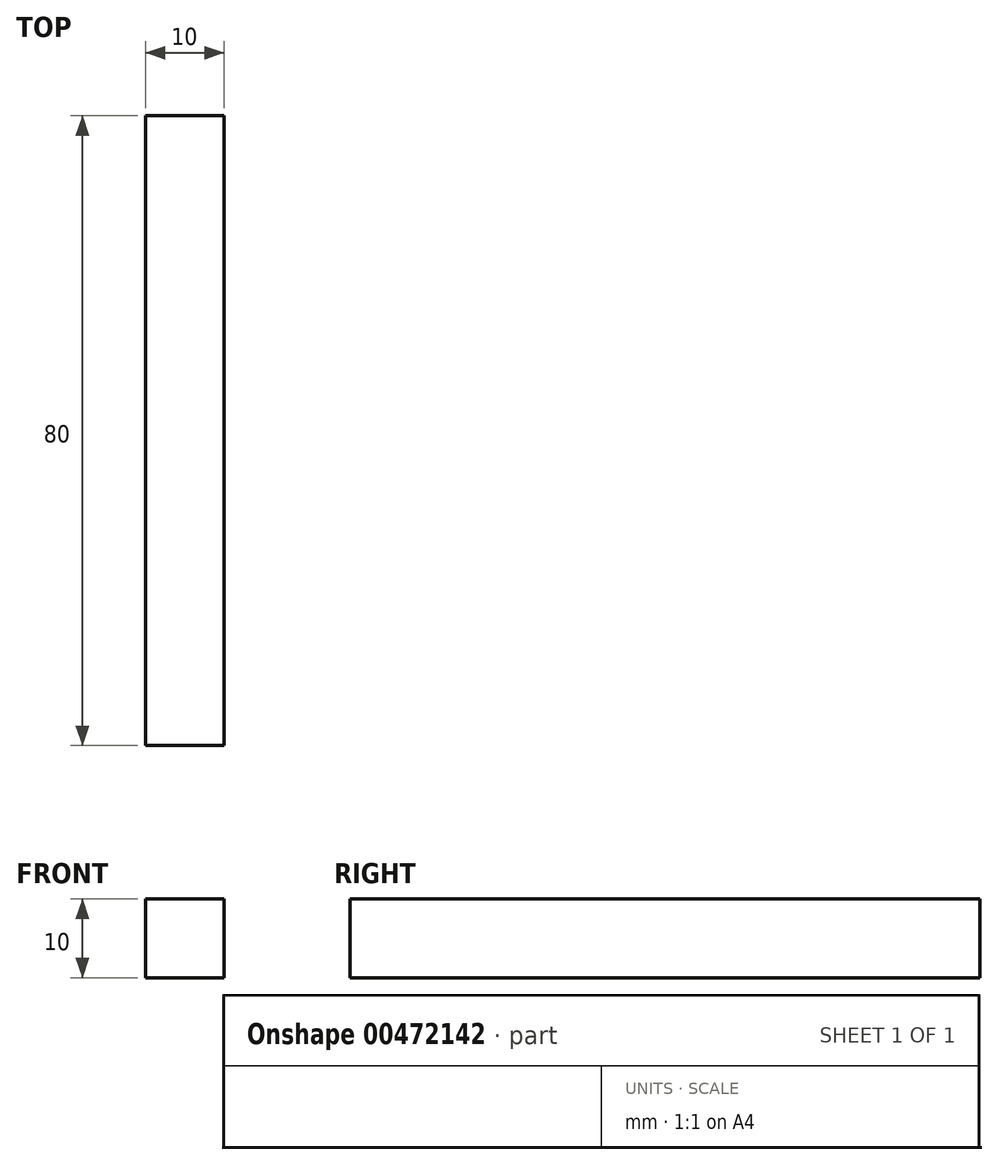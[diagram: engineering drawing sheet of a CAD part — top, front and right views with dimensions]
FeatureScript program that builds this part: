
annotation { "Feature Type Name" : "Feature", "Feature Type Description" : "" }
export const myFeature = defineFeature(function(context is Context, id is Id, definition is map)
    precondition{}
    {
        {
            var Q0;
            Q0=qCreatedBy(makeId("Front.planeOp"),FACE);
            var sketch = newSketch(context, id + "F0", { "sketchPlane" : qUnion([Q0])});
            skLineSegment(sketch, "E0.bottom", {"start": v(5, -5) * mm, "end": v(-5, -5) * mm});
            skLineSegment(sketch, "E0.top", {"start": v(5, 5) * mm, "end": v(-5, 5) * mm});
            skLineSegment(sketch, "E0.left", {"start": v(5, -5) * mm, "end": v(5, 5) * mm});
            skLineSegment(sketch, "E0.right", {"start": v(-5, -5) * mm, "end": v(-5, 5) * mm});
            skPoint(sketch, "E0.middle", {"position": v(0, 0) * mm});
            skSolve(sketch);
        }
        {
            var Q0;
            Q0=makeQuery(id+"F0.imprint","IMPRINT",FACE,{"disambiguationData":[TD([[makeQuery(id+"F0.imprint","IMPRINT",EDGE,{"derivedFrom":sQuery(id+"F0.wireOp",EDGE,"E0.bottom")}),-1.0]])]});
            extrude(context, id + "F1", {"entities" : qUnion([Q0]), "depth" : 80 * mm});
        }
    });
